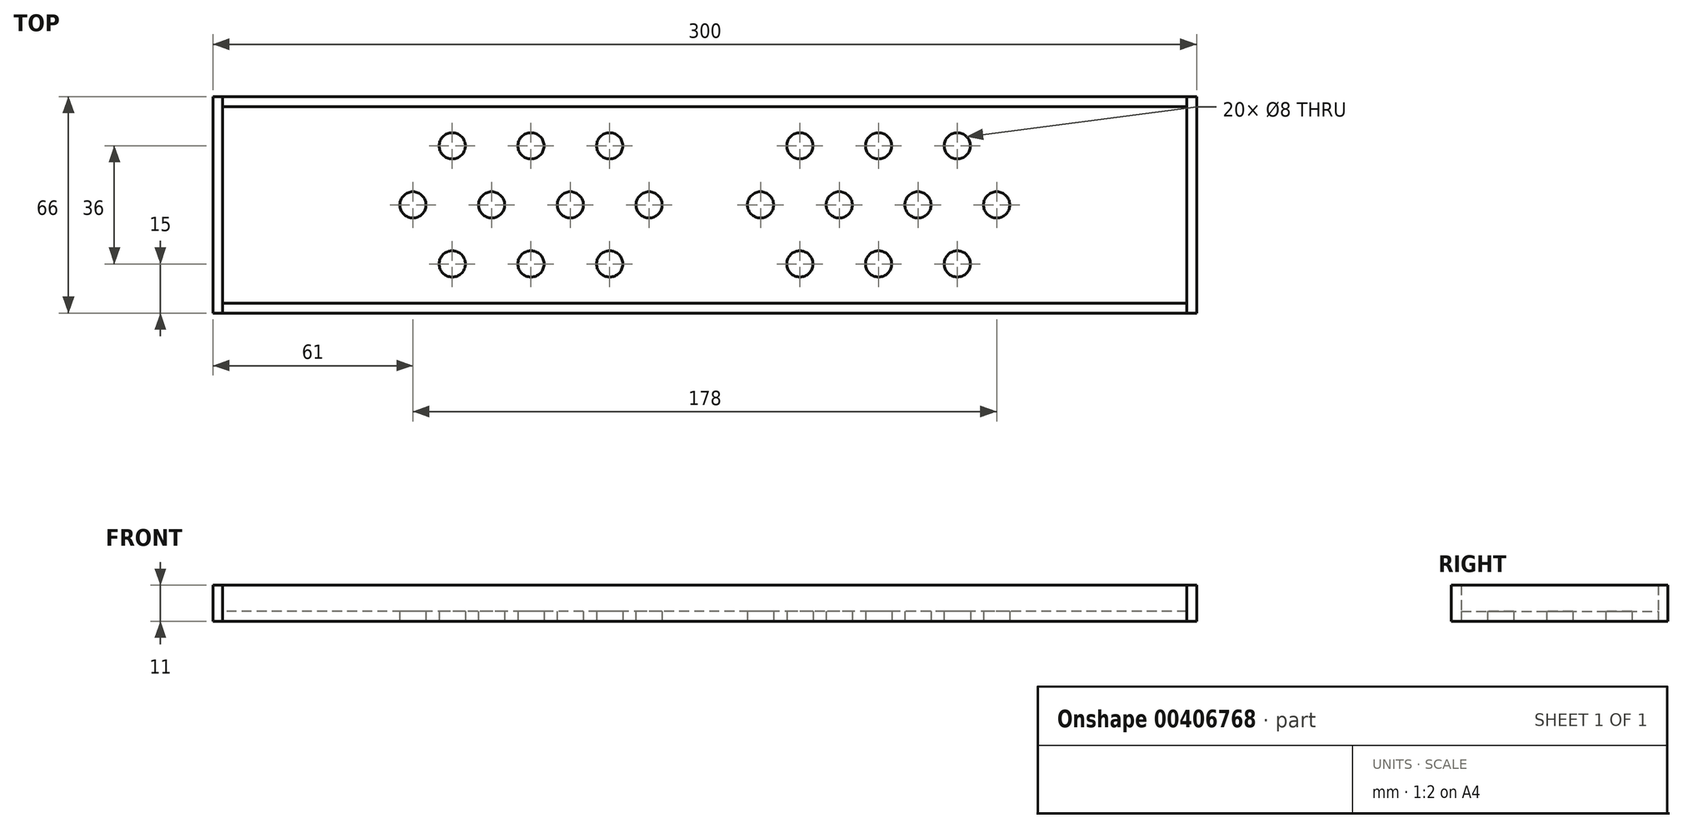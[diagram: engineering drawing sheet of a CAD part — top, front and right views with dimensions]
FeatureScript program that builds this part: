
annotation { "Feature Type Name" : "Feature", "Feature Type Description" : "" }
export const myFeature = defineFeature(function(context is Context, id is Id, definition is map)
    precondition{}
    {
        {
            var Q0;
            Q0=qCreatedBy(makeId("Top.planeOp"),FACE);
            var sketch = newSketch(context, id + "F0", { "sketchPlane" : qUnion([Q0])});
            skLineSegment(sketch, "E0.bottom", {"start": v(147, -30) * mm, "end": v(-147, -30) * mm});
            skLineSegment(sketch, "E0.top", {"start": v(147, 30) * mm, "end": v(-147, 30) * mm});
            skLineSegment(sketch, "E0.left", {"start": v(147, -30) * mm, "end": v(147, 30) * mm});
            skLineSegment(sketch, "E0.right", {"start": v(-147, -30) * mm, "end": v(-147, 30) * mm});
            skPoint(sketch, "E0.middle", {"position": v(0, 0) * mm});
            skLineSegment(sketch, "E1", {"start": v(0, 30) * mm, "end": v(0, -30) * mm, "construction": true});
            skLineSegment(sketch, "E2", {"start": v(-147, 0) * mm, "end": v(147, 0) * mm, "construction": true});
            skLineSegment(sketch, "E3", {"start": v(-17, 30) * mm, "end": v(-17, -30) * mm, "construction": true});
            skLineSegment(sketch, "E4", {"start": v(17, 30) * mm, "end": v(17, -30) * mm, "construction": true});
            skLineSegment(sketch, "E5", {"start": v(41, 30) * mm, "end": v(41, -30) * mm, "construction": true});
            skLineSegment(sketch, "E6", {"start": v(65, 30) * mm, "end": v(65, -30) * mm, "construction": true});
            skLineSegment(sketch, "E7", {"start": v(89, 30) * mm, "end": v(89, -30) * mm, "construction": true});
            skLineSegment(sketch, "E8", {"start": v(-41, 30) * mm, "end": v(-41, -30) * mm, "construction": true});
            skLineSegment(sketch, "E9", {"start": v(-65, 30) * mm, "end": v(-65, -30) * mm, "construction": true});
            skLineSegment(sketch, "E10", {"start": v(-89, 30) * mm, "end": v(-89, -30) * mm, "construction": true});
            skCircle(sketch, "E11", {"center": v(-89, 0) * mm, "radius": 10 * mm, "construction": true});
            skCircle(sketch, "E12", {"center": v(-65, 0) * mm, "radius": 10 * mm, "construction": true});
            skCircle(sketch, "E13", {"center": v(-41, 0) * mm, "radius": 10 * mm, "construction": true});
            skCircle(sketch, "E14", {"center": v(-17, 0) * mm, "radius": 10 * mm, "construction": true});
            skCircle(sketch, "E15", {"center": v(17, 0) * mm, "radius": 10 * mm, "construction": true});
            skCircle(sketch, "E16", {"center": v(41, 0) * mm, "radius": 10 * mm, "construction": true});
            skCircle(sketch, "E17", {"center": v(65, 0) * mm, "radius": 10 * mm, "construction": true});
            skCircle(sketch, "E18", {"center": v(89, 0) * mm, "radius": 10 * mm, "construction": true});
            skLineSegment(sketch, "E19", {"start": v(-77, 30) * mm, "end": v(-77, -30) * mm, "construction": true});
            skLineSegment(sketch, "E20", {"start": v(-53, 30) * mm, "end": v(-53, -30) * mm, "construction": true});
            skLineSegment(sketch, "E21", {"start": v(-29, 30) * mm, "end": v(-29, -30) * mm, "construction": true});
            skLineSegment(sketch, "E22", {"start": v(29, 30) * mm, "end": v(29, -30) * mm, "construction": true});
            skLineSegment(sketch, "E23", {"start": v(53, 30) * mm, "end": v(53, -30) * mm, "construction": true});
            skLineSegment(sketch, "E24", {"start": v(77, 30) * mm, "end": v(77, -30) * mm, "construction": true});
            skLineSegment(sketch, "E25", {"start": v(-147, -18) * mm, "end": v(147, -18) * mm, "construction": true});
            skCircle(sketch, "E26", {"center": v(-77, -18) * mm, "radius": 10 * mm, "construction": true});
            skCircle(sketch, "E27", {"center": v(-53, -18) * mm, "radius": 10 * mm, "construction": true});
            skCircle(sketch, "E28", {"center": v(-29, -18) * mm, "radius": 10 * mm, "construction": true});
            skCircle(sketch, "E29", {"center": v(29, -18) * mm, "radius": 10 * mm, "construction": true});
            skCircle(sketch, "E30", {"center": v(53, -18) * mm, "radius": 10 * mm, "construction": true});
            skCircle(sketch, "E31", {"center": v(77, -18) * mm, "radius": 10 * mm, "construction": true});
            skCircle(sketch, "E32", {"center": v(77, 18) * mm, "radius": 10 * mm, "construction": true});
            skCircle(sketch, "E33", {"center": v(53, 18) * mm, "radius": 10 * mm, "construction": true});
            skCircle(sketch, "E34", {"center": v(29, 18) * mm, "radius": 10 * mm, "construction": true});
            skCircle(sketch, "E35", {"center": v(-29, 18) * mm, "radius": 10 * mm, "construction": true});
            skCircle(sketch, "E36", {"center": v(-53, 18) * mm, "radius": 10 * mm, "construction": true});
            skCircle(sketch, "E37", {"center": v(-77, 18) * mm, "radius": 10 * mm, "construction": true});
            skCircle(sketch, "E38", {"center": v(-77, 18) * mm, "radius": 4 * mm});
            skCircle(sketch, "E39", {"center": v(-53, 18) * mm, "radius": 4 * mm});
            skCircle(sketch, "E40", {"center": v(-29, 18) * mm, "radius": 4 * mm});
            skCircle(sketch, "E41", {"center": v(29, 18) * mm, "radius": 4 * mm});
            skCircle(sketch, "E42", {"center": v(53, 18) * mm, "radius": 4 * mm});
            skCircle(sketch, "E43", {"center": v(77, 18) * mm, "radius": 4 * mm});
            skCircle(sketch, "E44", {"center": v(89, 0) * mm, "radius": 4 * mm});
            skCircle(sketch, "E45", {"center": v(65, 0) * mm, "radius": 4 * mm});
            skCircle(sketch, "E46", {"center": v(41, 0) * mm, "radius": 4 * mm});
            skCircle(sketch, "E47", {"center": v(17, 0) * mm, "radius": 4 * mm});
            skCircle(sketch, "E48", {"center": v(-17, 0) * mm, "radius": 4 * mm});
            skCircle(sketch, "E49", {"center": v(-41, 0) * mm, "radius": 4 * mm});
            skCircle(sketch, "E50", {"center": v(-65, 0) * mm, "radius": 4 * mm});
            skCircle(sketch, "E51", {"center": v(-89, 0) * mm, "radius": 4 * mm});
            skCircle(sketch, "E52", {"center": v(-77, -18) * mm, "radius": 4 * mm});
            skCircle(sketch, "E53", {"center": v(-53, -18) * mm, "radius": 4 * mm});
            skCircle(sketch, "E54", {"center": v(-29, -18) * mm, "radius": 4 * mm});
            skCircle(sketch, "E55", {"center": v(29, -18) * mm, "radius": 4 * mm});
            skCircle(sketch, "E56", {"center": v(53, -18) * mm, "radius": 4 * mm});
            skCircle(sketch, "E57", {"center": v(77, -18) * mm, "radius": 4 * mm});
            skLineSegment(sketch, "E58", {"start": v(-147, 18) * mm, "end": v(147, 18) * mm, "construction": true});
            skSolve(sketch);
        }
        {
            var Q0;
            Q0=makeQuery(id+"F0.imprint","IMPRINT",FACE,{"disambiguationData":[TD([[makeQuery(id+"F0.imprint","IMPRINT",EDGE,{"derivedFrom":sQuery(id+"F0.wireOp",EDGE,"E0.bottom")}),-1.0]])]});
            extrude(context, id + "F1", {"entities" : qUnion([Q0]), "depth" : 3 * mm});
        }
        {
            var Q0;
            Q0=makeQuery(id+"F1.opExtrude","CAP_FACE",FACE,{"disambiguationData":[OSD([sQuery(id+"F0.wireOp",EDGE,"E0.bottom"),sQuery(id+"F0.wireOp",EDGE,"E0.top"),sQuery(id+"F0.wireOp",EDGE,"E0.left"),sQuery(id+"F0.wireOp",EDGE,"E0.right"),sQuery(id+"F0.wireOp",EDGE,"E38"),sQuery(id+"F0.wireOp",EDGE,"E39"),sQuery(id+"F0.wireOp",EDGE,"E40"),sQuery(id+"F0.wireOp",EDGE,"E41"),sQuery(id+"F0.wireOp",EDGE,"E42"),sQuery(id+"F0.wireOp",EDGE,"E43"),sQuery(id+"F0.wireOp",EDGE,"E44"),sQuery(id+"F0.wireOp",EDGE,"E45"),sQuery(id+"F0.wireOp",EDGE,"E46"),sQuery(id+"F0.wireOp",EDGE,"E47"),sQuery(id+"F0.wireOp",EDGE,"E48"),sQuery(id+"F0.wireOp",EDGE,"E49"),sQuery(id+"F0.wireOp",EDGE,"E50"),sQuery(id+"F0.wireOp",EDGE,"E51"),sQuery(id+"F0.wireOp",EDGE,"E52"),sQuery(id+"F0.wireOp",EDGE,"E53"),sQuery(id+"F0.wireOp",EDGE,"E54"),sQuery(id+"F0.wireOp",EDGE,"E55"),sQuery(id+"F0.wireOp",EDGE,"E56"),sQuery(id+"F0.wireOp",EDGE,"E57")])],"isStart":true});
            var sketch = newSketch(context, id + "F2", { "sketchPlane" : qUnion([Q0])});
            skLineSegment(sketch, "E59", {"start": v(-147, 30) * mm, "end": v(-147, 33) * mm});
            skLineSegment(sketch, "E60", {"start": v(-147, 33) * mm, "end": v(147, 33) * mm});
            skLineSegment(sketch, "E61", {"start": v(147, 33) * mm, "end": v(147, 30) * mm});
            skLineSegment(sketch, "E62", {"start": v(-147, -30) * mm, "end": v(-147, -33) * mm});
            skLineSegment(sketch, "E63", {"start": v(-147, -33) * mm, "end": v(147, -33) * mm});
            skLineSegment(sketch, "E64", {"start": v(147, -33) * mm, "end": v(147, -30) * mm});
            skSolve(sketch);
        }
        {
            var Q0;
            Q0=makeQuery(id+"F2.imprint","IMPRINT",FACE,{"disambiguationData":[TD([[makeQuery(id+"F2.imprint","IMPRINT",EDGE,{"derivedFrom":sQuery(id+"F2.wireOp",EDGE,"E59")}),-1.0]])]});
            var Q1;
            Q1=makeQuery(id+"F2.imprint","IMPRINT",FACE,{"disambiguationData":[TD([[makeQuery(id+"F2.imprint","IMPRINT",EDGE,{"derivedFrom":sQuery(id+"F2.wireOp",EDGE,"E62")}),1.0]])]});
            var Q2;
            Q2=makeQuery(id+"F2.imprint","IMPRINT",FACE,{"disambiguationData":[TD([[makeQuery(id+"F2.imprint","IMPRINT",EDGE,{"derivedFrom":sQuery(id+"F2.wireOp",EDGE,"E59")}),1.0]])]});
            var Q3;
            Q3=makeQuery(id+"F2.imprint","IMPRINT",FACE,{"disambiguationData":[TD([[makeQuery(id+"F2.imprint","IMPRINT",EDGE,{"derivedFrom":sQuery(id+"F2.wireOp",EDGE,"E61")}),1.0]])]});
            extrude(context, id + "F3", {"entities" : qUnion([Q0, Q1, Q2, Q3]), "oppositeDirection" : true, "depth" : 11 * mm});
        }
        {
            var Q0;
            Q0=makeQuery(id+"F1.opExtrude","CAP_FACE",FACE,{"disambiguationData":[OSD([sQuery(id+"F0.wireOp",EDGE,"E0.bottom"),sQuery(id+"F0.wireOp",EDGE,"E0.top"),sQuery(id+"F0.wireOp",EDGE,"E0.left"),sQuery(id+"F0.wireOp",EDGE,"E0.right"),sQuery(id+"F0.wireOp",EDGE,"E38"),sQuery(id+"F0.wireOp",EDGE,"E39"),sQuery(id+"F0.wireOp",EDGE,"E40"),sQuery(id+"F0.wireOp",EDGE,"E41"),sQuery(id+"F0.wireOp",EDGE,"E42"),sQuery(id+"F0.wireOp",EDGE,"E43"),sQuery(id+"F0.wireOp",EDGE,"E44"),sQuery(id+"F0.wireOp",EDGE,"E45"),sQuery(id+"F0.wireOp",EDGE,"E46"),sQuery(id+"F0.wireOp",EDGE,"E47"),sQuery(id+"F0.wireOp",EDGE,"E48"),sQuery(id+"F0.wireOp",EDGE,"E49"),sQuery(id+"F0.wireOp",EDGE,"E50"),sQuery(id+"F0.wireOp",EDGE,"E51"),sQuery(id+"F0.wireOp",EDGE,"E52"),sQuery(id+"F0.wireOp",EDGE,"E53"),sQuery(id+"F0.wireOp",EDGE,"E54"),sQuery(id+"F0.wireOp",EDGE,"E55"),sQuery(id+"F0.wireOp",EDGE,"E56"),sQuery(id+"F0.wireOp",EDGE,"E57")])],"isStart":true});
            var sketch = newSketch(context, id + "F4", { "sketchPlane" : qUnion([Q0])});
            skLineSegment(sketch, "E65", {"start": v(147, 30) * mm, "end": v(147, 33) * mm});
            skLineSegment(sketch, "E66", {"start": v(147, 33) * mm, "end": v(150, 33) * mm});
            skLineSegment(sketch, "E67", {"start": v(150, 33) * mm, "end": v(150, -33) * mm});
            skLineSegment(sketch, "E68", {"start": v(150, -33) * mm, "end": v(147, -33) * mm});
            skLineSegment(sketch, "E69", {"start": v(147, -33) * mm, "end": v(147, -30) * mm});
            skLineSegment(sketch, "E70", {"start": v(-147, 30) * mm, "end": v(-147, 33) * mm});
            skLineSegment(sketch, "E71", {"start": v(-147, 33) * mm, "end": v(-150, 33) * mm});
            skLineSegment(sketch, "E72", {"start": v(-150, 33) * mm, "end": v(-150, -33) * mm});
            skLineSegment(sketch, "E73", {"start": v(-150, -33) * mm, "end": v(-147, -33) * mm});
            skLineSegment(sketch, "E74", {"start": v(-147, -33) * mm, "end": v(-147, -30) * mm});
            skSolve(sketch);
        }
        {
            var Q0;
            Q0=makeQuery(id+"F4.imprint","IMPRINT",FACE,{"disambiguationData":[TD([[makeQuery(id+"F4.imprint","IMPRINT",EDGE,{"derivedFrom":sQuery(id+"F4.wireOp",EDGE,"E70")}),1.0]])]});
            var Q1;
            Q1=makeQuery(id+"F4.imprint","IMPRINT",FACE,{"disambiguationData":[TD([[makeQuery(id+"F4.imprint","IMPRINT",EDGE,{"derivedFrom":sQuery(id+"F4.wireOp",EDGE,"E65")}),-1.0]])]});
            extrude(context, id + "F5", {"entities" : qUnion([Q0, Q1]), "oppositeDirection" : true, "depth" : 11 * mm});
        }
    });
